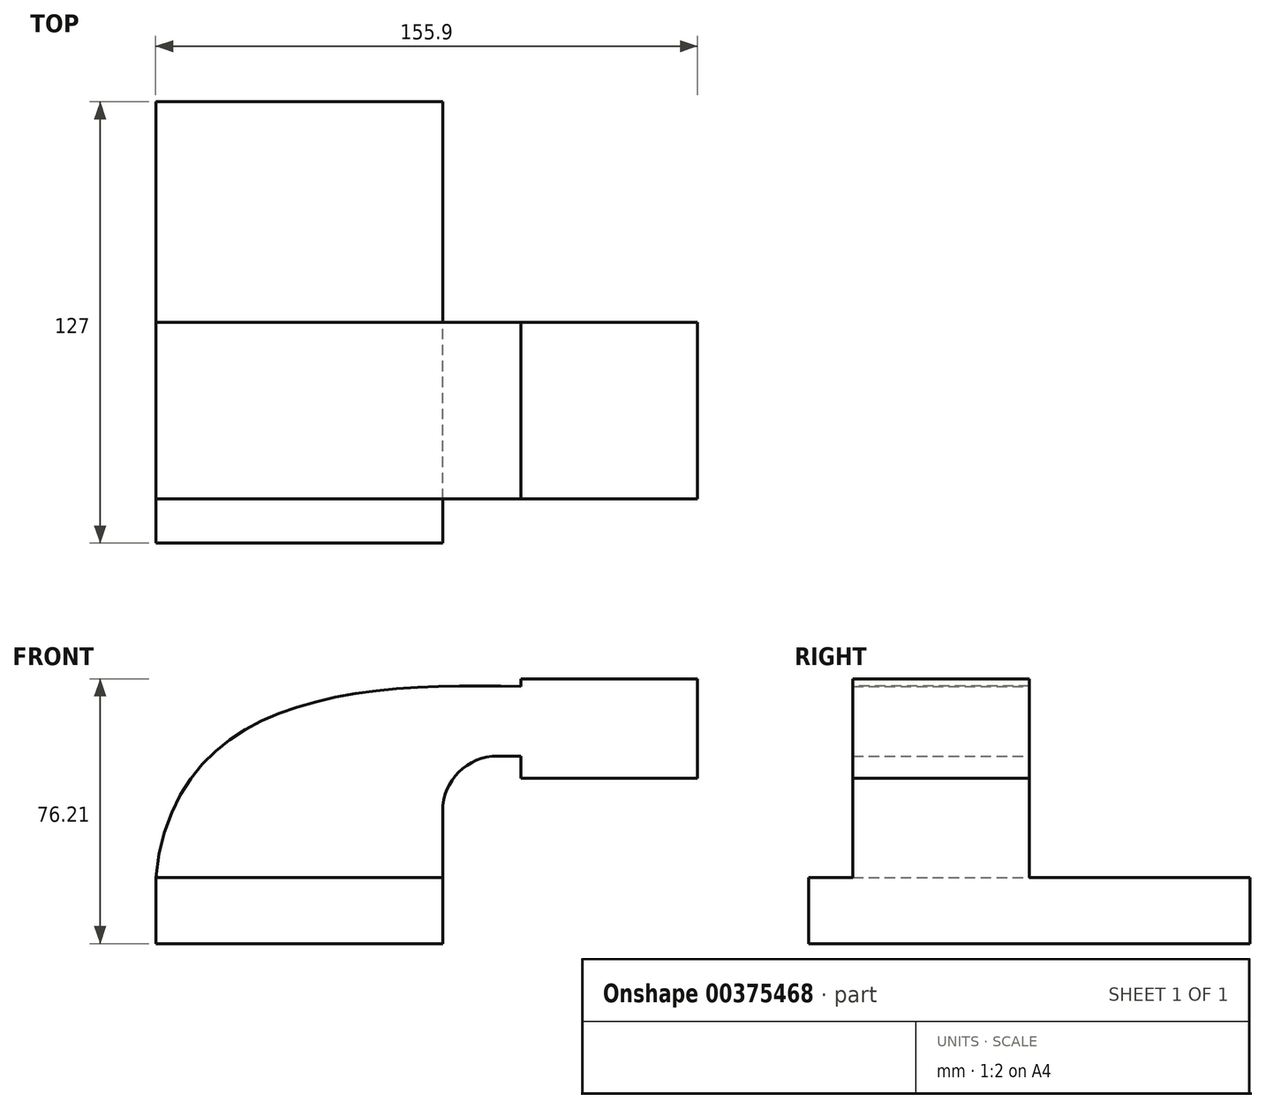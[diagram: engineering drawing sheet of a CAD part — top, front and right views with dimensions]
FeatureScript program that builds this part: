
annotation { "Feature Type Name" : "Feature", "Feature Type Description" : "" }
export const myFeature = defineFeature(function(context is Context, id is Id, definition is map)
    precondition{}
    {
        {
            var Q0;
            Q0=qCreatedBy(makeId("Front.planeOp"),FACE);
            var sketch = newSketch(context, id + "F0", { "sketchPlane" : qUnion([Q0])});
            skLineSegment(sketch, "E0.bottom", {"start": v(-41.28, -9.53) * mm, "end": v(41.28, -9.53) * mm});
            skLineSegment(sketch, "E0.top", {"start": v(-41.28, 9.53) * mm, "end": v(41.28, 9.53) * mm});
            skLineSegment(sketch, "E0.left", {"start": v(-41.28, -9.53) * mm, "end": v(-41.28, 9.53) * mm});
            skLineSegment(sketch, "E0.right", {"start": v(41.28, -9.53) * mm, "end": v(41.28, 9.53) * mm});
            skPoint(sketch, "E0.middle", {"position": v(0, 0) * mm});
            skLineSegment(sketch, "E1.bottom", {"start": v(63.82, 38.1) * mm, "end": v(114.62, 38.1) * mm});
            skLineSegment(sketch, "E1.top", {"start": v(63.82, 66.67) * mm, "end": v(114.62, 66.67) * mm});
            skLineSegment(sketch, "E1.left", {"start": v(63.82, 38.1) * mm, "end": v(63.82, 66.67) * mm});
            skLineSegment(sketch, "E1.right", {"start": v(114.62, 38.1) * mm, "end": v(114.62, 66.67) * mm});
            skPoint(sketch, "E1.middle", {"position": v(89.22, 52.39) * mm});
            skLineSegment(sketch, "E2", {"start": v(41.28, 9.52) * mm, "end": v(41.28, 28.57) * mm});
            skArc(sketch, "E3", {"start": v(41.27, 28.57) * mm, "mid": v(45.92, 39.8) * mm, "end": v(57.15, 44.45) * mm});
            skLineSegment(sketch, "E4", {"start": v(57.15, 44.45) * mm, "end": v(85.72, 44.45) * mm});
            skLineSegment(sketch, "E5.0", {"start": v(22.48, 9.52) * mm, "end": v(22.48, 47.05) * mm});
            skArc(sketch, "E6", {"start": v(22.48, 47.05) * mm, "mid": v(28.86, 60.47) * mm, "end": v(43.3, 64) * mm});
            skLineSegment(sketch, "E7", {"start": v(43.3, 64) * mm, "end": v(86.59, 64) * mm});
            skLineSegment(sketch, "E8", {"start": v(86.59, 64) * mm, "end": v(85.73, 44.45) * mm});
            skFitSpline(sketch, "E9", {"points": [v(-41.28, 9.53) * mm, v(86.59, 64) * mm], "startDerivative": vector(19.67, 192.05) * mm, "endDerivative": vector(134.96, -0.92) * mm});
            skSolve(sketch);
        }
        {
            var Q0;
            Q0=makeQuery(id+"F0.imprint","IMPRINT",FACE,{"disambiguationData":[TD([[makeQuery(id+"F0.imprint","IMPRINT",EDGE,{"derivedFrom":sQuery(id+"F0.wireOp",EDGE,"E0.bottom")}),1.0]])]});
            extrude(context, id + "F1", {"entities" : qUnion([Q0]), "endBound" : BoundingType.SYMMETRIC, "depth" : 127 * mm});
        }
        {
            var Q0;
            Q0 = qSketchRegion(id + "F0", true);
            extrude(context, id + "F2", {"entities" : qUnion([Q0]), "operationType" : NewBodyOperationType.ADD, "depth" : 50.8 * mm});
        }
    });
